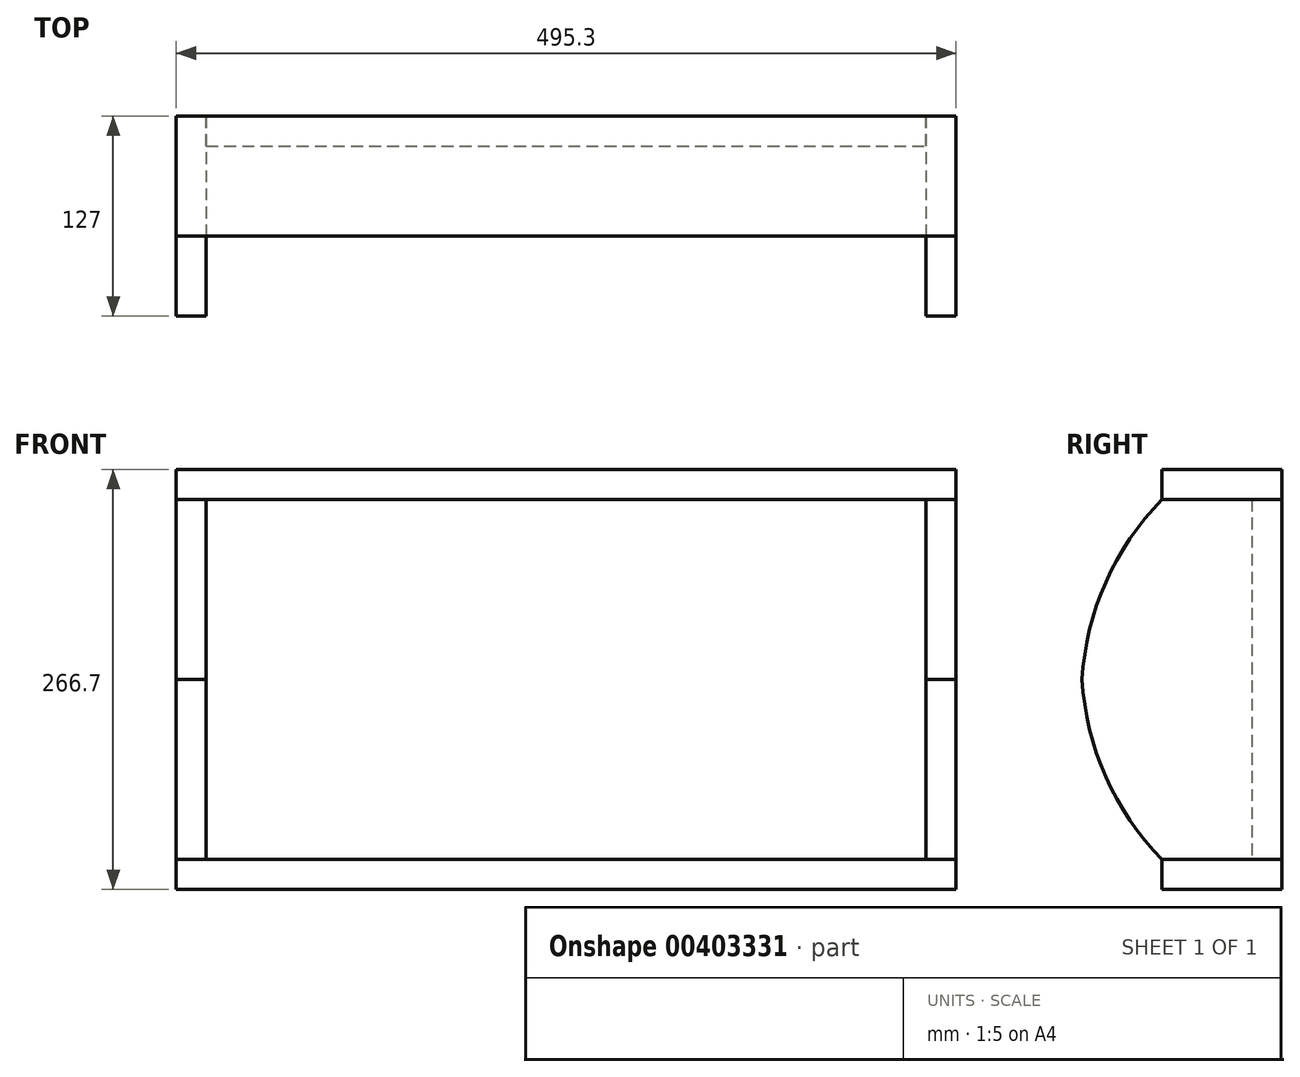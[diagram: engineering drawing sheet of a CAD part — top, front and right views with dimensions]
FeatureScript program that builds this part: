
annotation { "Feature Type Name" : "Feature", "Feature Type Description" : "" }
export const myFeature = defineFeature(function(context is Context, id is Id, definition is map)
    precondition{}
    {
        {
            var Q0;
            Q0=qCreatedBy(makeId("Right.planeOp"),FACE);
            var sketch = newSketch(context, id + "F0", { "sketchPlane" : qUnion([Q0])});
            skLineSegment(sketch, "E0.bottom", {"start": v(0, 114.3) * mm, "end": v(-76.2, 114.3) * mm});
            skLineSegment(sketch, "E0.top", {"start": v(0, -114.3) * mm, "end": v(-76.2, -114.3) * mm});
            skLineSegment(sketch, "E0.left", {"start": v(0, 114.3) * mm, "end": v(0, -114.3) * mm});
            skLineSegment(sketch, "E0.right", {"start": v(-76.2, 114.3) * mm, "end": v(-76.2, -114.3) * mm});
            skPoint(sketch, "E0.middle", {"position": v(-38.1, 0) * mm});
            skArc(sketch, "E1", {"start": v(-76.2, 114.3) * mm, "mid": v(-111.96, 61.76) * mm, "end": v(-127, 0) * mm});
            skArc(sketch, "E2.MirrorCS", {"start": v(-76.2, -114.3) * mm, "mid": v(-111.96, -61.76) * mm, "end": v(-127, 0) * mm});
            skSolve(sketch);
        }
        {
            var Q0;
            Q0 = qSketchRegion(id + "F0", true);
            extrude(context, id + "F1", {"entities" : qUnion([Q0]), "depth" : 19.05 * mm});
        }
        {
            var Q0;
            Q0=makeQuery(id+"F1.opExtrude","SWEPT_BODY",BODY,{"disambiguationData":[OSD([sQuery(id+"F0.wireOp",EDGE,"E0.bottom"),sQuery(id+"F0.wireOp",EDGE,"E0.top"),sQuery(id+"F0.wireOp",EDGE,"E0.left"),sQuery(id+"F0.wireOp",EDGE,"E1"),sQuery(id+"F0.wireOp",EDGE,"E2.MirrorCS")])]});
            transform(context, id + "F2", {"entities" : qUnion([Q0]), "transformType" : TransformType.TRANSLATION_3D, "dx" : 228.6 * mm, "dy" : 0 * mm, "dz" : 0 * mm, "makeCopy" : true});
        }
        {
            var Q0;
            Q0=makeQuery(id+"F1.opExtrude","SWEPT_BODY",BODY,{"disambiguationData":[OSD([sQuery(id+"F0.wireOp",EDGE,"E0.bottom"),sQuery(id+"F0.wireOp",EDGE,"E0.top"),sQuery(id+"F0.wireOp",EDGE,"E0.left"),sQuery(id+"F0.wireOp",EDGE,"E1"),sQuery(id+"F0.wireOp",EDGE,"E2.MirrorCS")])]});
            transform(context, id + "F3", {"entities" : qUnion([Q0]), "transformType" : TransformType.TRANSLATION_3D, "dx" : -247.65 * mm, "dy" : 0 * mm, "dz" : 0 * mm, "makeCopy" : false});
        }
        {
            var Q0;
            Q0=qCreatedBy(makeId("Front.planeOp"),FACE);
            var sketch = newSketch(context, id + "F4", { "sketchPlane" : qUnion([Q0])});
            skLineSegment(sketch, "E3.bottom", {"start": v(-228.6, 114.3) * mm, "end": v(228.6, 114.3) * mm});
            skLineSegment(sketch, "E3.top", {"start": v(-228.6, -114.3) * mm, "end": v(228.6, -114.3) * mm});
            skLineSegment(sketch, "E3.left", {"start": v(-228.6, 114.3) * mm, "end": v(-228.6, -114.3) * mm});
            skLineSegment(sketch, "E3.right", {"start": v(228.6, 114.3) * mm, "end": v(228.6, -114.3) * mm});
            skPoint(sketch, "E3.middle", {"position": v(0, 0) * mm});
            skSolve(sketch);
        }
        {
            var Q0;
            Q0 = qSketchRegion(id + "F4", true);
            extrude(context, id + "F5", {"entities" : qUnion([Q0]), "depth" : 19.05 * mm});
        }
        {
            var Q0;
            Q0=qCreatedBy(makeId("Top.planeOp"),FACE);
            var sketch = newSketch(context, id + "F6", { "sketchPlane" : qUnion([Q0])});
            skLineSegment(sketch, "E4.bottom", {"start": v(247.65, 0) * mm, "end": v(-247.65, 0) * mm});
            skLineSegment(sketch, "E4.top", {"start": v(247.65, -76.2) * mm, "end": v(-247.65, -76.2) * mm});
            skLineSegment(sketch, "E4.left", {"start": v(247.65, 0) * mm, "end": v(247.65, -76.2) * mm});
            skLineSegment(sketch, "E4.right", {"start": v(-247.65, 0) * mm, "end": v(-247.65, -76.2) * mm});
            skSolve(sketch);
        }
        {
            var Q0;
            Q0 = qSketchRegion(id + "F6", true);
            extrude(context, id + "F7", {"entities" : qUnion([Q0]), "depth" : 19.05 * mm});
        }
        {
            var Q0;
            Q0=makeQuery(id+"F7.opExtrude","SWEPT_BODY",BODY,{"disambiguationData":[OSD([sQuery(id+"F6.wireOp",EDGE,"E4.bottom"),sQuery(id+"F6.wireOp",EDGE,"E4.top"),sQuery(id+"F6.wireOp",EDGE,"E4.left"),sQuery(id+"F6.wireOp",EDGE,"E4.right")])]});
            transform(context, id + "F8", {"entities" : qUnion([Q0]), "transformType" : TransformType.TRANSLATION_3D, "dx" : 0 * mm, "dy" : 0 * mm, "dz" : 114.3 * mm, "makeCopy" : true});
        }
        {
            var Q0;
            Q0=makeQuery(id+"F7.opExtrude","SWEPT_BODY",BODY,{"disambiguationData":[OSD([sQuery(id+"F6.wireOp",EDGE,"E4.bottom"),sQuery(id+"F6.wireOp",EDGE,"E4.top"),sQuery(id+"F6.wireOp",EDGE,"E4.left"),sQuery(id+"F6.wireOp",EDGE,"E4.right")])]});
            transform(context, id + "F9", {"entities" : qUnion([Q0]), "transformType" : TransformType.TRANSLATION_3D, "dx" : 0 * mm, "dy" : 0 * mm, "dz" : -133.35 * mm, "makeCopy" : false});
        }
    });
